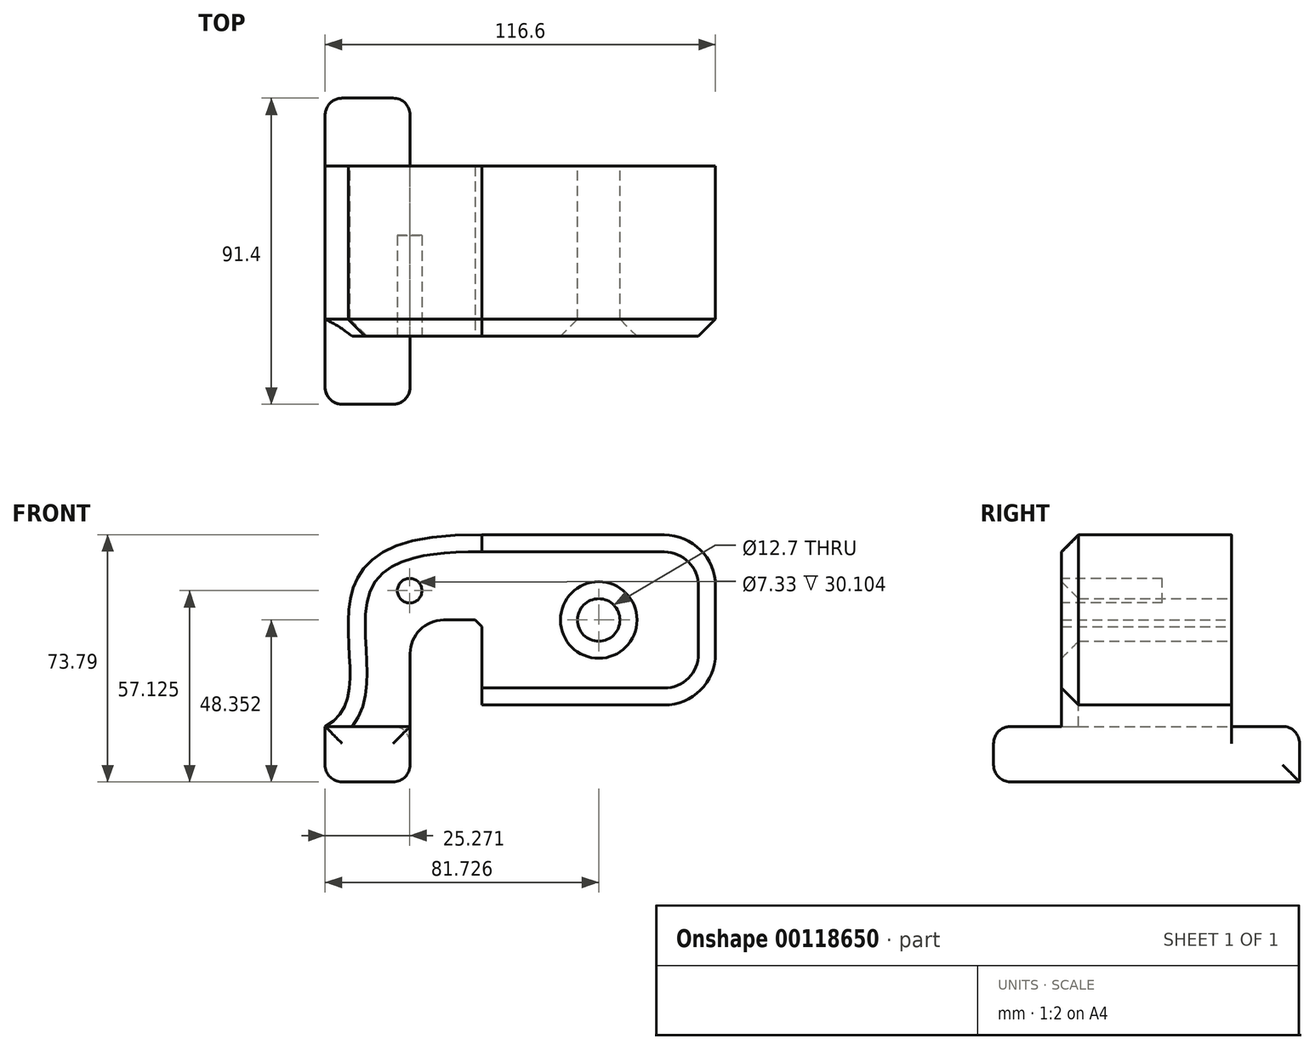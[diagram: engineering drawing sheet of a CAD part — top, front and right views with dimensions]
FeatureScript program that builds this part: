
annotation { "Feature Type Name" : "Feature", "Feature Type Description" : "" }
export const myFeature = defineFeature(function(context is Context, id is Id, definition is map)
    precondition{}
    {
        {
            var Q0;
            Q0=qCreatedBy(makeId("Front.planeOp"),FACE);
            var sketch = newSketch(context, id + "F0", { "sketchPlane" : qUnion([Q0])});
            skLineSegment(sketch, "E0.bottom", {"start": v(12.7, 8.29) * mm, "end": v(-12.7, 8.29) * mm});
            skLineSegment(sketch, "E0.top", {"start": v(12.7, -8.29) * mm, "end": v(-12.7, -8.29) * mm});
            skLineSegment(sketch, "E0.left", {"start": v(12.7, 8.29) * mm, "end": v(12.7, -8.29) * mm});
            skLineSegment(sketch, "E0.right", {"start": v(-12.7, 8.29) * mm, "end": v(-12.7, -8.29) * mm});
            skPoint(sketch, "E0.middle", {"position": v(0, 0) * mm});
            skLineSegment(sketch, "E1", {"start": v(12.7, 8.29) * mm, "end": v(12.7, 30.04) * mm});
            skArc(sketch, "E2", {"start": v(12.7, 30.04) * mm, "mid": v(15.64, 37.13) * mm, "end": v(22.73, 40.06) * mm});
            skLineSegment(sketch, "E3.bottom", {"start": v(103.9, 14.66) * mm, "end": v(34.16, 14.66) * mm});
            skLineSegment(sketch, "E3.top", {"start": v(103.9, 65.46) * mm, "end": v(34.16, 65.46) * mm});
            skLineSegment(sketch, "E3.left", {"start": v(103.9, 14.66) * mm, "end": v(103.9, 65.46) * mm});
            skLineSegment(sketch, "E3.right", {"start": v(34.16, 14.66) * mm, "end": v(34.16, 65.46) * mm});
            skPoint(sketch, "E3.middle", {"position": v(69.03, 40.06) * mm});
            skLineSegment(sketch, "E4", {"start": v(22.73, 40.06) * mm, "end": v(34.16, 40.06) * mm});
            skLineSegment(sketch, "E5.0", {"start": v(22.73, 53.04) * mm, "end": v(34.16, 53.04) * mm});
            skArc(sketch, "E5.1", {"start": v(-0.28, 30.04) * mm, "mid": v(6.46, 46.3) * mm, "end": v(22.73, 53.04) * mm});
            skLineSegment(sketch, "E5.2", {"start": v(-0.28, 9.55) * mm, "end": v(-0.28, 30.04) * mm});
            skFitSpline(sketch, "E6", {"points": [v(-12.7, 8.29) * mm, v(34.16, 65.46) * mm], "startDerivative": vector(66.58, 32.1) * mm, "endDerivative": vector(198.27, -4.54) * mm});
            skCircle(sketch, "E7", {"center": v(69.03, 40.06) * mm, "radius": 6.35 * mm});
            skSolve(sketch);
        }
        {
            var Q0;
            Q0=makeQuery(id+"F0.imprint","IMPRINT",FACE,{"disambiguationData":[TD([[makeQuery(id+"F0.imprint","IMPRINT",EDGE,{"derivedFrom":sQuery(id+"F0.wireOp",EDGE,"E0.bottom")}),1.0]])]});
            extrude(context, id + "F1", {"entities" : qUnion([Q0]), "flatOperationType" : FlatOperationType.REMOVE, "endBound" : BoundingType.SYMMETRIC, "offsetDistance" : 25.4 * mm, "depth" : 91.4 * mm, "domain" : OperationDomain.MODEL});
        }
        {
            var Q0;
            Q0=makeQuery(id+"F0.imprint","IMPRINT",FACE,{"disambiguationData":[TD([[makeQuery(id+"F0.imprint","IMPRINT",EDGE,{"derivedFrom":sQuery(id+"F0.wireOp",EDGE,"E0.bottom")}),-1.0]])]});
            extrude(context, id + "F2", {"entities" : qUnion([Q0]), "operationType" : NewBodyOperationType.ADD, "endBound" : BoundingType.SYMMETRIC, "depth" : 25.4 * mm});
        }
        {
            var Q0;
            Q0 = qSketchRegion(id + "F0", true);
            extrude(context, id + "F3", {"entities" : qUnion([Q0]), "operationType" : NewBodyOperationType.ADD, "endBound" : BoundingType.SYMMETRIC, "depth" : 50.8 * mm});
        }
        {
            var Q0;
            Q0=makeQuery(id+"F3.opExtrude","SWEPT_EDGE",EDGE,{"disambiguationData":[OSD([sQuery(id+"F0.wireOp",EDGE,"E3.top"),sQuery(id+"F0.wireOp",EDGE,"E3.left")])]});
            var Q1;
            Q1=makeQuery(id+"F3.opExtrude","SWEPT_EDGE",EDGE,{"disambiguationData":[OSD([sQuery(id+"F0.wireOp",EDGE,"E3.bottom"),sQuery(id+"F0.wireOp",EDGE,"E3.left")])]});
            fillet(context, id + "F4", {"entities" : qUnion([Q0, Q1]), "radius" : 15.29 * mm, "tangentPropagation" : true, "allowEdgeOverflow" : false});
        }
        {
            var Q0;
            Q0=makeQuery(id+"F3.opExtrude","CAP_EDGE",EDGE,{"disambiguationData":[OSD([sQuery(id+"F0.wireOp",EDGE,"E6")])],"isStart":false});
            var Q1;
            {var subQ0=sQuery(id+"F0.wireOp",EDGE,"E3.left");var subQ1=sQuery(id+"F0.wireOp",EDGE,"E3.top");Q1=makeQuery(id+"F4.opFillet","BLEND_EDGE",EDGE,{"blendedFrom":[makeQuery(id+"F3.opExtrude","SWEPT_EDGE",EDGE,{"disambiguationData":[OSD([subQ1,subQ0])]}),makeQuery(id+"F3.opExtrude","CAP_FACE",FACE,{"disambiguationData":[OSD([sQuery(id+"F0.wireOp",EDGE,"E0.top"),sQuery(id+"F0.wireOp",EDGE,"E0.left"),sQuery(id+"F0.wireOp",EDGE,"E0.right"),sQuery(id+"F0.wireOp",EDGE,"E1"),sQuery(id+"F0.wireOp",EDGE,"E2"),sQuery(id+"F0.wireOp",EDGE,"E3.bottom"),subQ1,subQ0,sQuery(id+"F0.wireOp",EDGE,"E3.right"),sQuery(id+"F0.wireOp",EDGE,"E4"),sQuery(id+"F0.wireOp",EDGE,"E6"),sQuery(id+"F0.wireOp",EDGE,"E7")])],"isStart":false})],"blendedInto":[makeQuery(id+"F3.opExtrude","CAP_FACE",FACE,{"disambiguationData":[OSD([sQuery(id+"F0.wireOp",EDGE,"E0.top"),sQuery(id+"F0.wireOp",EDGE,"E0.left"),sQuery(id+"F0.wireOp",EDGE,"E0.right"),sQuery(id+"F0.wireOp",EDGE,"E1"),sQuery(id+"F0.wireOp",EDGE,"E2"),sQuery(id+"F0.wireOp",EDGE,"E3.bottom"),subQ1,subQ0,sQuery(id+"F0.wireOp",EDGE,"E3.right"),sQuery(id+"F0.wireOp",EDGE,"E4"),sQuery(id+"F0.wireOp",EDGE,"E6"),sQuery(id+"F0.wireOp",EDGE,"E7")])],"isStart":false})]});}
            var Q2;
            Q2=makeQuery(id+"F3.opExtrude","CAP_EDGE",EDGE,{"disambiguationData":[OSD([sQuery(id+"F0.wireOp",EDGE,"E7")])],"isStart":false});
            chamfer(context, id + "F5", {"entities" : qUnion([Q0, Q1, Q2]), "width" : 5.08 * mm, "tangentPropagation" : true});
        }
        {
            var Q0;
            Q0=makeQuery(id+"F5.opChamfer","SPLIT",FACE,{"disambiguationData":[OD(0.0)],"derivedFrom":makeQuery(id+"F3.opExtrude","CAP_FACE",FACE,{"disambiguationData":[OSD([sQuery(id+"F0.wireOp",EDGE,"E0.top"),sQuery(id+"F0.wireOp",EDGE,"E0.left"),sQuery(id+"F0.wireOp",EDGE,"E0.right"),sQuery(id+"F0.wireOp",EDGE,"E1"),sQuery(id+"F0.wireOp",EDGE,"E2"),sQuery(id+"F0.wireOp",EDGE,"E3.bottom"),sQuery(id+"F0.wireOp",EDGE,"E3.top"),sQuery(id+"F0.wireOp",EDGE,"E3.left"),sQuery(id+"F0.wireOp",EDGE,"E3.right"),sQuery(id+"F0.wireOp",EDGE,"E4"),sQuery(id+"F0.wireOp",EDGE,"E6"),sQuery(id+"F0.wireOp",EDGE,"E7")])],"isStart":false})});
            var sketch = newSketch(context, id + "F6", { "sketchPlane" : qUnion([Q0])});
            skCircle(sketch, "E8", {"center": v(12.57, 48.83) * mm, "radius": 3.66 * mm});
            skSolve(sketch);
        }
        {
            var Q0;
            Q0=makeQuery(id+"F6.imprint","IMPRINT",FACE,{"disambiguationData":[TD([[makeQuery(id+"F6.imprint","IMPRINT",EDGE,{"derivedFrom":sQuery(id+"F6.wireOp",EDGE,"E8")}),1.0]])]});
            extrude(context, id + "F7", {"entities" : qUnion([Q0]), "operationType" : NewBodyOperationType.REMOVE, "oppositeDirection" : true, "depth" : 30.1 * mm});
        }
        {
            var Q0;
            Q0=makeQuery(id+"F7.boolean.opBoolean","COPY",EDGE,{"derivedFrom":makeQuery(id+"F7.opExtrude","CAP_EDGE",EDGE,{"disambiguationData":[OSD([sQuery(id+"F6.wireOp",EDGE,"E8")])],"isStart":true})});
            var Q1;
            {var subQ0=sQuery(id+"F0.wireOp",EDGE,"E4");var subQ1=sQuery(id+"F0.wireOp",EDGE,"E3.right");Q1=makeQuery(id+"F3.boolean.opBoolean","MERGE",EDGE,{"derivedFrom":[makeQuery(id+"F2.opExtrude","SWEPT_EDGE",EDGE,{"disambiguationData":[OSD([subQ1,subQ0])]}),makeQuery(id+"F3.opExtrude","SWEPT_EDGE",EDGE,{"disambiguationData":[OSD([subQ1,subQ0])]})]});}
            chamfer(context, id + "F8", {"entities" : qUnion([Q0, Q1]), "width" : 2 * mm, "tangentPropagation" : true});
        }
        {
            var Q0;
            Q0=makeQuery(id+"F1.opExtrude","CAP_EDGE",EDGE,{"disambiguationData":[OSD([sQuery(id+"F0.wireOp",EDGE,"E0.bottom")])],"isStart":true});
            var Q1;
            Q1=makeQuery(id+"F1.opExtrude","CAP_EDGE",EDGE,{"disambiguationData":[OSD([sQuery(id+"F0.wireOp",EDGE,"E0.bottom")])],"isStart":false});
            var Q2;
            Q2=makeQuery(id+"F1.opExtrude","CAP_EDGE",EDGE,{"disambiguationData":[OSD([sQuery(id+"F0.wireOp",EDGE,"E0.right")])],"isStart":true});
            var Q3;
            Q3=makeQuery(id+"F1.opExtrude","CAP_EDGE",EDGE,{"disambiguationData":[OSD([sQuery(id+"F0.wireOp",EDGE,"E0.right")])],"isStart":false});
            var Q4;
            Q4=makeQuery(id+"F1.opExtrude","CAP_FACE",FACE,{"disambiguationData":[OSD([sQuery(id+"F0.wireOp",EDGE,"E0.bottom"),sQuery(id+"F0.wireOp",EDGE,"E0.top"),sQuery(id+"F0.wireOp",EDGE,"E0.left"),sQuery(id+"F0.wireOp",EDGE,"E0.right")])],"isStart":false});
            var Q5;
            Q5=makeQuery(id+"F1.opExtrude","CAP_EDGE",EDGE,{"disambiguationData":[OSD([sQuery(id+"F0.wireOp",EDGE,"E0.left")])],"isStart":true});
            var Q6;
            {var subQ0=sQuery(id+"F0.wireOp",EDGE,"E1");var subQ1=sQuery(id+"F0.wireOp",EDGE,"E0.bottom");var subQ2=sQuery(id+"F0.wireOp",EDGE,"E0.left");Q6=makeQuery(id+"F2.boolean.opBoolean","SPLIT",EDGE,{"disambiguationData":[TD([makeQuery(id+"F1.opExtrude","CAP_FACE",FACE,{"disambiguationData":[OSD([subQ1,sQuery(id+"F0.wireOp",EDGE,"E0.top"),subQ2,sQuery(id+"F0.wireOp",EDGE,"E0.right")])],"isStart":true})])],"derivedFrom":makeQuery(id+"F1.opExtrude","SWEPT_EDGE",EDGE,{"disambiguationData":[OSD([subQ1,subQ2,subQ0])]})});}
            var Q7;
            Q7=makeQuery(id+"F1.opExtrude","SWEPT_EDGE",EDGE,{"disambiguationData":[OSD([sQuery(id+"F0.wireOp",EDGE,"E0.top"),sQuery(id+"F0.wireOp",EDGE,"E0.left")])]});
            var Q8;
            Q8=makeQuery(id+"F1.opExtrude","SWEPT_EDGE",EDGE,{"disambiguationData":[OSD([sQuery(id+"F0.wireOp",EDGE,"E0.top"),sQuery(id+"F0.wireOp",EDGE,"E0.right")])]});
            fillet(context, id + "F9", {"entities" : qUnion([Q0, Q1, Q2, Q3, Q4, Q5, Q6, Q7, Q8]), "radius" : 5.08 * mm, "tangentPropagation" : true, "allowEdgeOverflow" : false});
        }
    });
